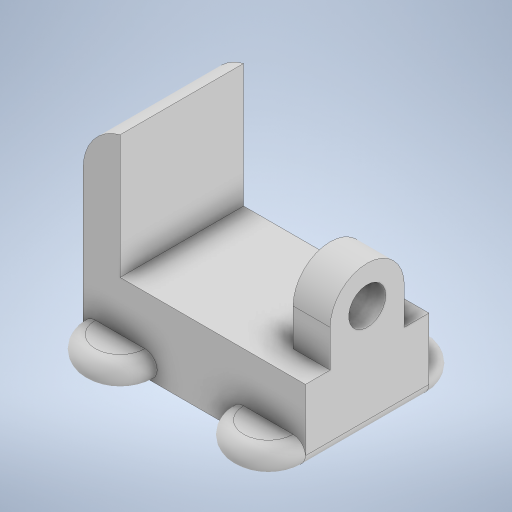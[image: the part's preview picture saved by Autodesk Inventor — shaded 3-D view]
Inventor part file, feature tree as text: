
AUTODESK INVENTOR PART (.ipt)
format: ipt  version: 2024 (Build 280153000, 153)  size: 318,976 bytes
history: native  units: mm
features: sketch x5, extrude x4, other x2, fillet x2
ambient origin geometry x8: Origin, YZ Plane, XZ Plane, XY Plane, X Axis, Y Axis, Z Axis, Center Point
bodies: Solid1 (feature_tree)
feature tree (13):
  extrude  "Extrusion1"  Depth=90.0mm
  extrude  "Extrusion2"  Depth=75.0mm
  sketch  "Sketch3"  dims[d4=50.0mm d5=20.0mm]
  extrude  "Extrusion3"  Depth=20.0mm
  other  "Full Round Fillet2"
  extrude  "Extrusion4"  Depth=15.0mm
  other  "Full Round Fillet4"
  fillet  "Fillet1"  Radius=25.0mm
  fillet  "Fillet2"  Radius=15.0mm
  sketch  "Sketch1"  dims[d0=60.0mm d1=90.0mm]
  sketch  "Sketch2"  dims[d2=30.0mm d3=75.0mm]
  sketch  "Sketch5"  dims[d6=50.0mm d7=0.0mm d10=45.0mm d11=25.0mm d13=15.0mm]
  sketch  "Sketch7"  dims[d14=15.0mm d15=15.0mm d16=0.0mm d18=30.0mm d19=10.0mm d20=0.0mm d21=30.0mm d22=30.0mm d23=10.0mm d24=0.0mm d25=5.0mm d26=5.0mm]
